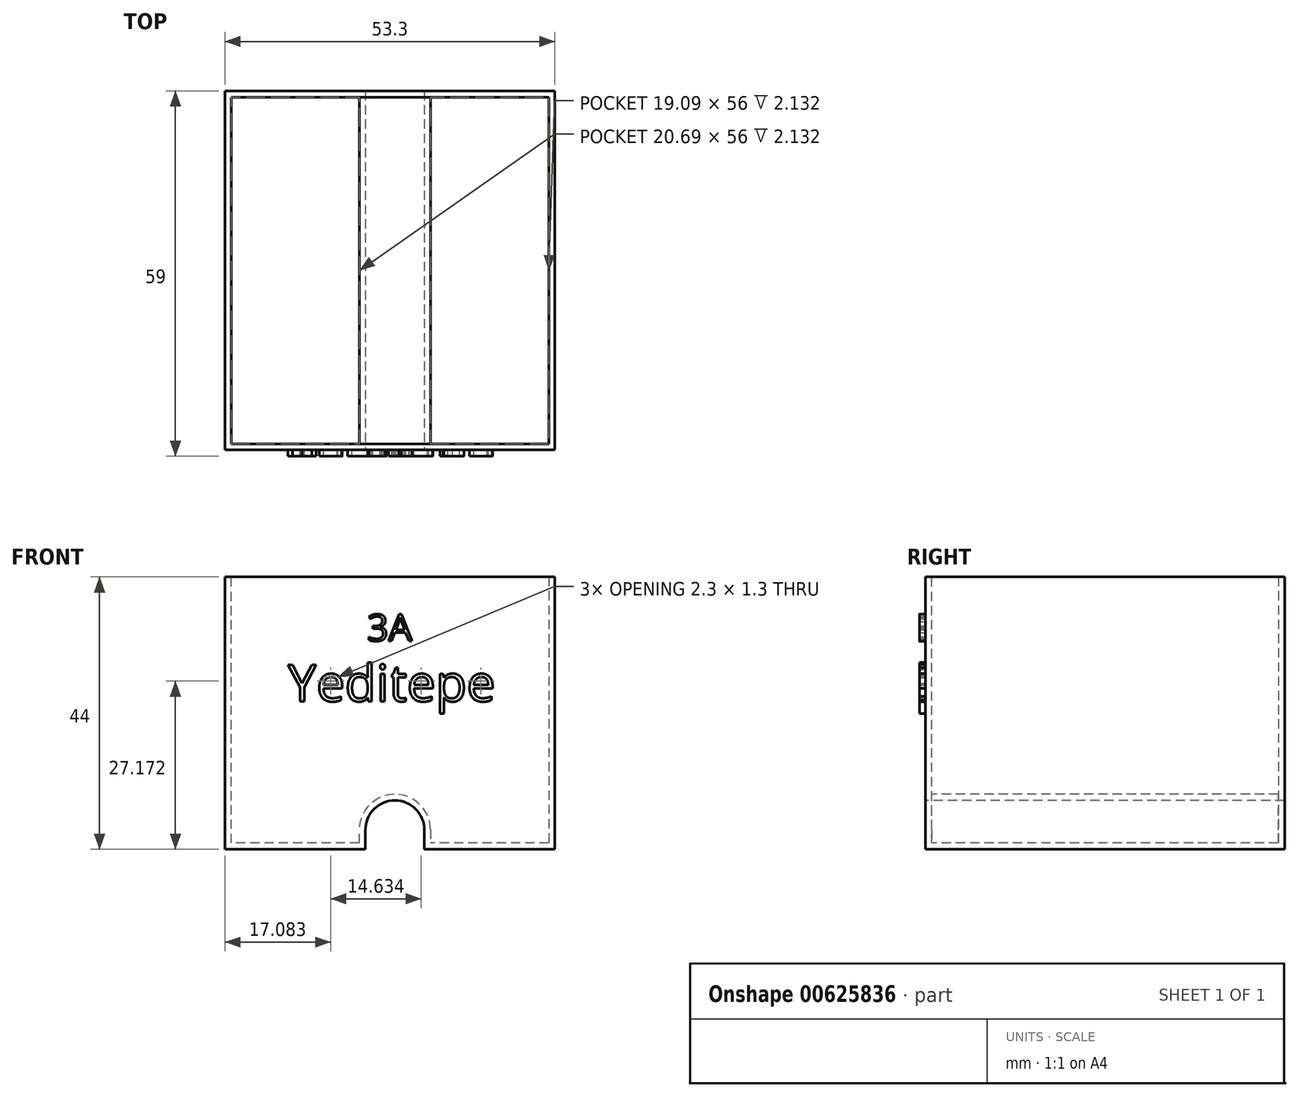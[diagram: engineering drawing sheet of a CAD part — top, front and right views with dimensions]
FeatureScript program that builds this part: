
annotation { "Feature Type Name" : "Feature", "Feature Type Description" : "" }
export const myFeature = defineFeature(function(context is Context, id is Id, definition is map)
    precondition{}
    {
        {
            var Q0;
            Q0=qCreatedBy(makeId("Front.planeOp"),FACE);
            var sketch = newSketch(context, id + "F0", { "sketchPlane" : qUnion([Q0])});
            skLineSegment(sketch, "E0", {"start": v(0, 0) * mm, "end": v(0, 44) * mm});
            skLineSegment(sketch, "E1", {"start": v(0, 44) * mm, "end": v(53.3, 44) * mm});
            skLineSegment(sketch, "E2", {"start": v(53.3, 44) * mm, "end": v(53.3, 0) * mm});
            skLineSegment(sketch, "E3", {"start": v(53.3, 0) * mm, "end": v(0, 0) * mm});
            skSolve(sketch);
        }
        {
            var Q0;
            Q0=makeQuery(id+"F0.imprint","IMPRINT",FACE,{"disambiguationData":[TD([[makeQuery(id+"F0.imprint","IMPRINT",EDGE,{"derivedFrom":sQuery(id+"F0.wireOp",EDGE,"E0")}),-1.0]])]});
            var sketch = newSketch(context, id + "F1", { "sketchPlane" : qUnion([Q0])});
            skPoint(sketch, "E4", {"position": v(27.45, 0) * mm});
            skPoint(sketch, "E5", {"position": v(27.56, 4.4) * mm});
            skLineSegment(sketch, "E6", {"start": v(27.45, 0) * mm, "end": v(22.69, 0) * mm});
            skLineSegment(sketch, "E7", {"start": v(22.69, 0) * mm, "end": v(22.69, 3.13) * mm});
            skLineSegment(sketch, "E8", {"start": v(32.2, 3.13) * mm, "end": v(32.2, 0) * mm});
            skLineSegment(sketch, "E9", {"start": v(32.2, 0) * mm, "end": v(27.45, 0) * mm});
            skPoint(sketch, "E10", {"position": v(53.24, 0) * mm});
            skArc(sketch, "E11", {"start": v(22.69, 3.13) * mm, "mid": v(27.45, 7.9) * mm, "end": v(32.2, 3.13) * mm});
            skSolve(sketch);
        }
        {
            var Q0;
            Q0=makeQuery(id+"F0.imprint","IMPRINT",FACE,{"disambiguationData":[TD([[makeQuery(id+"F0.imprint","IMPRINT",EDGE,{"derivedFrom":sQuery(id+"F0.wireOp",EDGE,"E0")}),-1.0]])]});
            extrude(context, id + "F2", {"entities" : qUnion([Q0]), "oppositeDirection" : true, "depth" : 58 * mm, "offsetDistance" : 25 * mm});
        }
        {
            var Q0;
            {var subQ0=sQuery(id+"F1.wireOp",EDGE,"o3UlRvsk-wD0c-Z0cn-f8Ce-j1c1HLYsYfFA");Q0=makeQuery(id+"F1.imprint","IMPRINT",FACE,{"disambiguationData":[TD([[makeQuery(id+"F1.imprint","IMPRINT",EDGE,{"derivedFrom":subQ0}),1.0]])]});}
            var Q1;
            Q1=makeQuery(id+"F1.imprint","IMPRINT",FACE,{"disambiguationData":[TD([[makeQuery(id+"F1.imprint","IMPRINT",EDGE,{"derivedFrom":sQuery(id+"F1.wireOp",EDGE,"E6")}),-1.0]])]});
            extrude(context, id + "F3", {"entities" : qUnion([Q0, Q1]), "operationType" : NewBodyOperationType.REMOVE, "endBound" : BoundingType.THROUGH_ALL, "oppositeDirection" : true, "depth" : 58 * mm, "offsetDistance" : 25 * mm});
        }
        {
            var Q0;
            Q0=makeQuery(id+"F2.opExtrude","SWEPT_FACE",FACE,{"disambiguationData":[OSD([sQuery(id+"F0.wireOp",EDGE,"E1")])]});
            shell(context, id + "F4", {"entities" : qUnion([Q0]), "thickness" : 1 * mm});
        }
        {
            var Q0;
            Q0=makeQuery(id+"F2.opExtrude","CAP_FACE",FACE,{"disambiguationData":[OSD([sQuery(id+"F0.wireOp",EDGE,"E0"),sQuery(id+"F0.wireOp",EDGE,"E1"),sQuery(id+"F0.wireOp",EDGE,"E2"),sQuery(id+"F0.wireOp",EDGE,"E3")])],"isStart":true});
            var sketch = newSketch(context, id + "F5", { "sketchPlane" : qUnion([Q0])});
            skText(sketch, "E12", { "text": "Yeditepe\n", "fontName": "OpenSans-Regular.ttf"});
            skLineSegment(sketch, "E13", {"start": v(27.45, 7.9) * mm, "end": v(26.65, 44) * mm, "construction": true});
            skLineSegment(sketch, "E14", {"start": v(27.45, 7.9) * mm, "end": v(26.65, 44) * mm});
            const initialGuessF5  = {"E12": [0.01016, 0.0239, 1, 0, 0.00592]};
            skSetInitialGuess(sketch, initialGuessF5);
            skSolve(sketch);
        }
        {
            var Q0;
            Q0=makeQuery(id+"F5.imprint","IMPRINT",FACE,{"disambiguationData":[TD([[makeQuery(id+"F5.imprint","IMPRINT",EDGE,{"derivedFrom":sQuery(id+"F5.wireOp",EDGE,"E12.sketch_text.stroke-0")}),-1.0]])]});
            var Q1;
            Q1=makeQuery(id+"F5.imprint","IMPRINT",FACE,{"disambiguationData":[TD([[makeQuery(id+"F5.imprint","IMPRINT",EDGE,{"derivedFrom":sQuery(id+"F5.wireOp",EDGE,"E12.sketch_text.stroke-9")}),-1.0]])]});
            var Q2;
            Q2=makeQuery(id+"F5.imprint","IMPRINT",FACE,{"disambiguationData":[TD([[makeQuery(id+"F5.imprint","IMPRINT",EDGE,{"derivedFrom":sQuery(id+"F5.wireOp",EDGE,"E12.sketch_text.stroke-28")}),-1.0]])]});
            var Q3;
            Q3=makeQuery(id+"F5.imprint","IMPRINT",FACE,{"disambiguationData":[TD([[makeQuery(id+"F5.imprint","IMPRINT",EDGE,{"derivedFrom":sQuery(id+"F5.wireOp",EDGE,"E12.sketch_text.stroke-52")}),-1.0]])]});
            var Q4;
            Q4=makeQuery(id+"F5.imprint","IMPRINT",FACE,{"disambiguationData":[TD([[makeQuery(id+"F5.imprint","IMPRINT",EDGE,{"derivedFrom":sQuery(id+"F5.wireOp",EDGE,"E12.sketch_text.stroke-56")}),-1.0]])]});
            var Q5;
            Q5=makeQuery(id+"F5.imprint","IMPRINT",FACE,{"disambiguationData":[TD([[makeQuery(id+"F5.imprint","IMPRINT",EDGE,{"derivedFrom":sQuery(id+"F5.wireOp",EDGE,"E12.sketch_text.stroke-64")}),-1.0]])]});
            var Q6;
            Q6=makeQuery(id+"F5.imprint","IMPRINT",FACE,{"disambiguationData":[TD([[makeQuery(id+"F5.imprint","IMPRINT",EDGE,{"derivedFrom":sQuery(id+"F5.wireOp",EDGE,"E12.sketch_text.stroke-83")}),-1.0]])]});
            var Q7;
            Q7=makeQuery(id+"F5.imprint","IMPRINT",FACE,{"disambiguationData":[TD([[makeQuery(id+"F5.imprint","IMPRINT",EDGE,{"derivedFrom":sQuery(id+"F5.wireOp",EDGE,"E12.sketch_text.stroke-102")}),-1.0]])]});
            var Q8;
            Q8=makeQuery(id+"F5.imprint","IMPRINT",FACE,{"disambiguationData":[TD([[makeQuery(id+"F5.imprint","IMPRINT",EDGE,{"derivedFrom":sQuery(id+"F5.wireOp",EDGE,"E12.sketch_text.stroke-127")}),-1.0]])]});
            extrude(context, id + "F6", {"entities" : qUnion([Q0, Q1, Q2, Q3, Q4, Q5, Q6, Q7, Q8]), "depth" : 1 * mm, "offsetDistance" : 25 * mm});
        }
        {
            var Q0;
            {var subQ0=sQuery(id+"F0.wireOp",EDGE,"E2");var subQ1=sQuery(id+"F0.wireOp",EDGE,"E1");var subQ2=sQuery(id+"F0.wireOp",EDGE,"E3");var subQ3=sQuery(id+"F0.wireOp",EDGE,"E0");Q0=makeQuery(id+"F6.boolean.opBoolean","SPLIT",FACE,{"disambiguationData":[TD([makeQuery(id+"F2.opExtrude","SWEPT_FACE",FACE,{"disambiguationData":[OSD([subQ3])]})])],"derivedFrom":makeQuery(id+"F2.opExtrude","CAP_FACE",FACE,{"disambiguationData":[OSD([subQ3,subQ1,subQ0,subQ2])],"isStart":true})});}
            var sketch = newSketch(context, id + "F7", { "sketchPlane" : qUnion([Q0])});
            skText(sketch, "E15", { "text": "3A\n", "fontName": "OpenSans-Regular.ttf"});
            const initialGuessF7  = {"E15": [0.02297, 0.03365, 1, 0, 0.00433]};
            skSetInitialGuess(sketch, initialGuessF7);
            skSolve(sketch);
        }
        {
            var Q0;
            Q0 = qSketchRegion(id + "F7", true);
            extrude(context, id + "F8", {"entities" : qUnion([Q0]), "depth" : 1 * mm, "offsetDistance" : 25 * mm});
        }
    });
